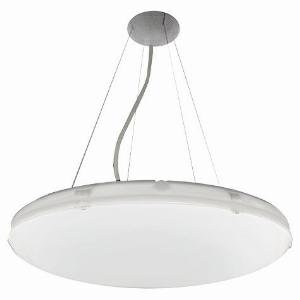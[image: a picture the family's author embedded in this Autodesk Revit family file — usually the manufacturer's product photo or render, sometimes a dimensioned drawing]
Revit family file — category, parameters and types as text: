
# Revit family: 3f_filippi_-_3f_petra_sospensione_3f_filippi_-_34411_-_3f_petra_op_620_50w_led_so
name_source: partatom
category: Lighting Fixtures
units: mm (PartAtom-declared; Revit-internal decimal feet)

## family parameters
Cut with Voids When Loaded = No
Host = Face
Light Source = No
Part Type = Normal
Room Calculation Point = No
Round Connector Dimension = Use Diameter
Shared = No

## types (1)
- 3F Filippi - 3F Petra Sospensione (1 x LED, 5955 lm, 53 W, 4000 K)
    Apparent Load = 53 VA
    Approval mark = ENEC
    CIE Flux Codes = 45 76 93 92 100
    Color Rendering = 80
    Color Temperature = 4000 K
    Control Gear = Electronic ballast
    Default Elevation = 1800 mm
    Description = ILLUMINOTECHNICAL
Luminous efficiency 100% (DLOR 92%, ULOR 8%).
Initial luminous flux of the luminaire 5955 lm.
Diffused symmetric distribution.
Installation Interdistance Transv.D = 1.25 x hu - Long.D = 1.25 x hu.
Tabular UGR (CIE 117 - 4H-8H; S=0.25H; 70/50/20): RUG 20.6 - 20.6.
Beam angle: 115° - 114°.
Luminous efficacy 112 lm/W.
Lifetime (L93/B10): 30000 h. (tq+25°C)
Lifetime (L90/B10): 50000 h. (tq+25°C)
Lifetime (L85/B10): 80000 h. (tq+25°C)
Lifetime (L80/B10): 100000 h. (tq+25°C)
Sudden decreased luminous flux after 50000 hours: 0% (C0).
Photobiological safety in compliance with IEC/TR 62778: RG0 risk exempt, (IEC 62471).
In compliance with IEC/EN 62722-2-1 - IEC/EN 62717 standards.

SOURCE
Circular LED module 50W/840.
Energy efficiency class (UE 2019/2020 - UE 2019/2015): D.
CIE 13.3 Colour rendering index: CRI >80 (R9 <50%).
IES TM-30 Fidelity Index: Rf = 84 Rg = 95.
CCT nominal colour temperature 4000 K.
Colour initial tolerance (MacAdam): SDCM 3.

MECHANICAL
Housing in glazed self-extinguishing V2 polycarbonate, UV stabilised, injection moulded.
Ecologic anti-aging injected sealing gasket.
Gear-tray reflector unit in aluminium, painted in white epoxy-polyester, fixed to the housing by quick-fastening steel devices, hinged opening.
Diffuser in opal methacrylate (PMMA), injection moulded.
Snug fit safety snap-lock clips for diffuser mounting in transparent polycarbonate, screwdriver opening.
Adjustable suspension with Rose in white polycarbonate, with stainless steel cables, 2 m long.
Luminaire with limited surface temperature. - D - (EN 60598-2-24)
Dimensions: diameter 620 mm, height 134 mm. Weight 5.535 kg.
IP65 protection degree.
Mechanical strength to impacts IK02 (0.2 joule).
Glow-wire test resistance 650°C.

ELECTRICAL
Halogen Free electronic wiring 230V-50/60Hz, power factor 0.95, THD <25%, constant output current, SELV, class I, 1 driver.
Power of the luminaire 53 W.
CE - IEC 60598-1 - EN 60598-1.
SAFE FLICKER: PstLM=<1 and SVM=<0.4 (IEC TR 61547-1 and IEC TR 63158), to ensure a more comfortable and safe light.
Luminaire compliant with EN 60598-2-22 for power supply from a centralised emergency system CPSS (Central Power Supply System), not incorporated in the luminaire - high risk areas excluded. The default power and flux are 100% in AC and 100% in DC.
Ambient temperature from 0°C to +25°C.
Temperature class T6 max 85°C.
Relative humidity UR: <85%.

INSTALLATION
Suspended.

APPLICATIONS
Transit areas, stairwells. Environments where a diffused lighting provides visual comfort.
Virtually in all environments compatibly with the emissions/atmospheres compromising the use of plastic materials.
Not suitable for installation on surfaces subject to important vibrations, exposed to weather conditions.

WARNING
Luminaire designed for disposal/recycling at end-of-life.
Replaceable (LED only) light source by a professional. Replaceable control gear by a professional.
    Height = 134 mm
    Lamp = 1 x LED
    Lamp Light Flux = 5955 lm
    Lamp Power = 53 W
    Lamp count = 1
    Length = 620 mm
    Lifetime = 50000 h
    Luminous efficacy = 112 lm/W
    Manufacturer = 3F Filippi
    ModVariant = No
    Model = 3F Filippi - 34411 - 3F Petra OP 620 50W LED SO
    Mounting Place = Ceiling
    Mounting Type = Pendant
    Number of Poles = 1
    OnlyDefault = Yes
    Power Factor = 1
    Product Name = 3F Filippi - 3F Petra Sospensione
    Product group = pendant luminaire
    ProductGroupID = 9
    Protection Class = Protection class I
    Protection Degree = IP 65
    RLX_Detail_Level = 1
    RLX_Emergency_Light_Flux = 0 lm
    RLX_Emergency_Type = 0
    RLX_Emergency_Type_DB = No
    RlxData = <blob elided: 229893 chars, md5=525641aa>
    Socket = socket
    Standby Power = 0 W
    System Light Flux = 5955 lm
    System Power = 53 W
    Type Comments = Product without accessories
    Type Image = 3ffilippi_3f_petra_sospensione.jpg
    URL = http://relux.com
    VarID = ---
    Voltage = 0 V
    Weight = 0.00 kg
    Width = 0 mm  [stored 0 ft]

note: [stored X ft] marks values corroborated as IEEE doubles in the binary element streams (Revit-internal decimal feet)

## geometry (parser evidence)
native form markers: Blend x4, Sweep x12
no freeform markers — native parametric forms only
